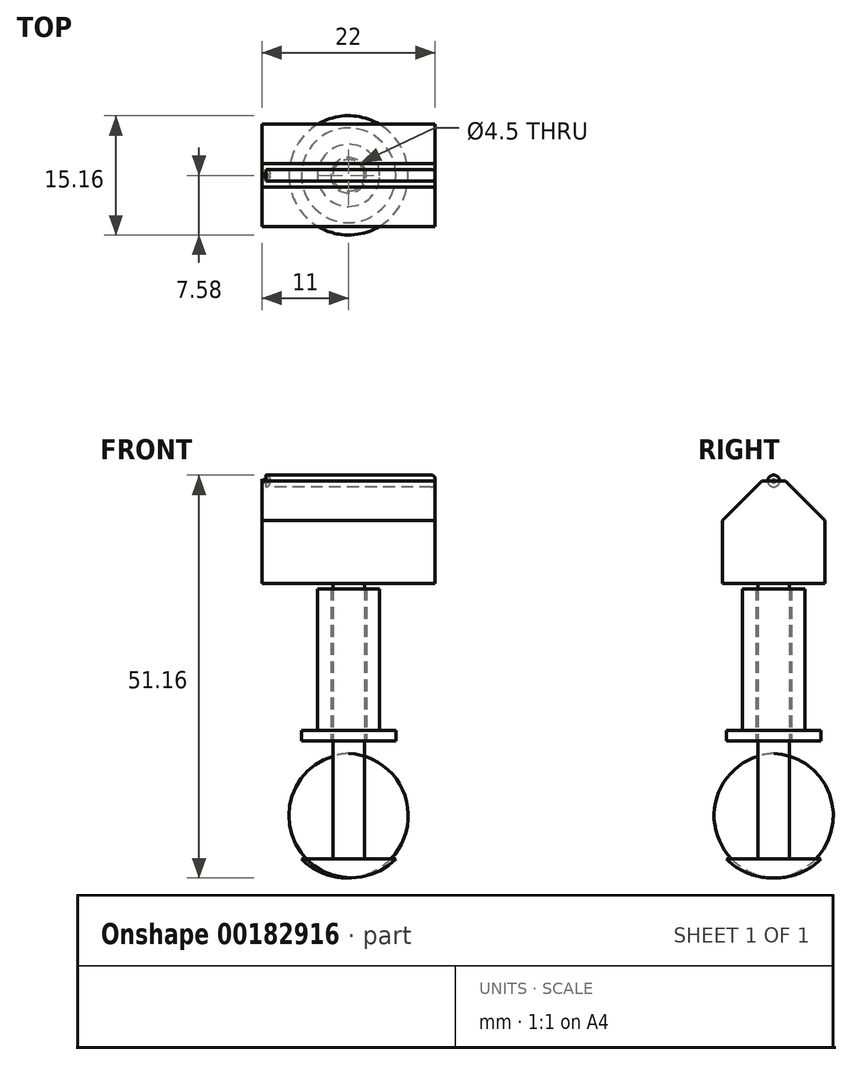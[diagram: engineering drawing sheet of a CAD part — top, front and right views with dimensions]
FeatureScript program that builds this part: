
annotation { "Feature Type Name" : "Feature", "Feature Type Description" : "" }
export const myFeature = defineFeature(function(context is Context, id is Id, definition is map)
    precondition{}
    {
        {
            var Q0;
            Q0=qCreatedBy(makeId("Top.planeOp"),FACE);
            var sketch = newSketch(context, id + "F0", { "sketchPlane" : qUnion([Q0])});
            skCircle(sketch, "E0", {"center": v(0, 0) * mm, "radius": 2 * mm});
            skSolve(sketch);
        }
        {
            var Q0;
            Q0 = qSketchRegion(id + "F0", true);
            extrude(context, id + "F1", {"entities" : qUnion([Q0]), "depth" : 40 * mm});
        }
        {
            var Q0;
            Q0=qCreatedBy(makeId("Right.planeOp"),FACE);
            var sketch = newSketch(context, id + "F2", { "sketchPlane" : qUnion([Q0])});
            skLineSegment(sketch, "E1", {"start": v(0, 0) * mm, "end": v(-6, 0) * mm});
            skLineSegment(sketch, "E2", {"start": v(0, 0) * mm, "end": v(0, -2.4) * mm});
            skArc(sketch, "E3", {"start": v(-6, 0) * mm, "mid": v(-3.26, -1.84) * mm, "end": v(0, -2.4) * mm});
            skSolve(sketch);
        }
        {
            var Q0;
            Q0=makeQuery(id+"F2.imprint","IMPRINT",FACE,{"disambiguationData":[TD([[makeQuery(id+"F2.imprint","IMPRINT",EDGE,{"derivedFrom":sQuery(id+"F2.wireOp",EDGE,"E1")}),1.0]])]});
            var Q1;
            Q1=sQuery(id+"F2.wireOp",EDGE,"E2");
            revolve(context, id + "F3", {"operationType" : NewBodyOperationType.ADD, "entities" : qUnion([Q0]), "axis" : qUnion([Q1]), "revolveType" : RevolveType.FULL});
        }
        {
            var Q0;
            Q0=makeQuery(id+"F1.opExtrude","CAP_FACE",FACE,{"disambiguationData":[OSD([sQuery(id+"F0.wireOp",EDGE,"E0")])],"isStart":false});
            var sketch = newSketch(context, id + "F4", { "sketchPlane" : qUnion([Q0])});
            skLineSegment(sketch, "E4.bottom", {"start": v(11, -6.5) * mm, "end": v(-11, -6.5) * mm});
            skLineSegment(sketch, "E4.top", {"start": v(11, 6.5) * mm, "end": v(-11, 6.5) * mm});
            skLineSegment(sketch, "E4.left", {"start": v(11, -6.5) * mm, "end": v(11, 6.5) * mm});
            skLineSegment(sketch, "E4.right", {"start": v(-11, -6.5) * mm, "end": v(-11, 6.5) * mm});
            skPoint(sketch, "E4.middle", {"position": v(0, 0) * mm});
            skSolve(sketch);
        }
        {
            var Q0;
            Q0=makeQuery(id+"F4.imprint","IMPRINT",FACE,{"disambiguationData":[TD([[makeQuery(id+"F4.imprint","IMPRINT",EDGE,{"derivedFrom":sQuery(id+"F4.wireOp",EDGE,"E4.bottom")}),-1.0]])]});
            extrude(context, id + "F5", {"entities" : qUnion([Q0]), "oppositeDirection" : true, "depth" : 5 * mm});
        }
        {
            var Q0;
            Q0=makeQuery(id+"F5.opExtrude","CAP_FACE",FACE,{"disambiguationData":[OSD([sQuery(id+"F0.wireOp",EDGE,"E0"),sQuery(id+"F4.wireOp",EDGE,"E4.bottom"),sQuery(id+"F4.wireOp",EDGE,"E4.top"),sQuery(id+"F4.wireOp",EDGE,"E4.left"),sQuery(id+"F4.wireOp",EDGE,"E4.right")])],"isStart":true});
            var Q1;
            Q1=makeQuery(id+"F1.opExtrude","CAP_FACE",FACE,{"disambiguationData":[OSD([sQuery(id+"F0.wireOp",EDGE,"E0")])],"isStart":false});
            extrude(context, id + "F6", {"entities" : qUnion([Q0, Q1]), "operationType" : NewBodyOperationType.ADD, "depth" : 8 * mm});
        }
        {
            var Q0;
            Q0=makeQuery(id+"F6.opExtrude","CAP_EDGE",EDGE,{"disambiguationData":[OSD([sQuery(id+"F4.wireOp",EDGE,"E4.bottom")])],"isStart":false});
            var Q1;
            Q1=makeQuery(id+"F6.opExtrude","CAP_EDGE",EDGE,{"disambiguationData":[OSD([sQuery(id+"F4.wireOp",EDGE,"E4.top")])],"isStart":false});
            chamfer(context, id + "F7", {"entities" : qUnion([Q0, Q1]), "width" : 5 * mm, "tangentPropagation" : true});
        }
        {
            var Q0;
            Q0=qCreatedBy(makeId("Right.planeOp"),FACE);
            var sketch = newSketch(context, id + "F8", { "sketchPlane" : qUnion([Q0])});
            skCircle(sketch, "E5", {"center": v(0, 48) * mm, "radius": 0.75 * mm});
            skSolve(sketch);
        }
        {
            var Q0;
            Q0=makeQuery(id+"F8.imprint","IMPRINT",FACE,{"disambiguationData":[TD([[makeQuery(id+"F8.imprint","IMPRINT",EDGE,{"derivedFrom":sQuery(id+"F8.wireOp",EDGE,"E5")}),1.0]])]});
            extrude(context, id + "F9", {"entities" : qUnion([Q0]), "depth" : 11 * mm, "hasSecondDirection" : true, "secondDirectionOppositeDirection" : true, "secondDirectionDepth" : 11 * mm});
        }
        {
            var Q0;
            Q0=makeQuery(id+"F9.opExtrude","CAP_EDGE",EDGE,{"disambiguationData":[OSD([sQuery(id+"F8.wireOp",EDGE,"E5")])],"isStart":false});
            var Q1;
            Q1=makeQuery(id+"F9.opExtrude","CAP_EDGE",EDGE,{"disambiguationData":[OSD([sQuery(id+"F8.wireOp",EDGE,"E5")])],"isStart":true});
            fillet(context, id + "F10", {"entities" : qUnion([Q0, Q1]), "radius" : 0.5 * mm, "tangentPropagation" : true, "allowEdgeOverflow" : false});
        }
        {
            var Q0;
            Q0=qCreatedBy(makeId("Top.planeOp"),FACE);
            cPlane(context, id + "F11", {"entities" : qUnion([Q0]), "cplaneType" : CPlaneType.OFFSET, "offset" : 15 * mm, "width" : 150 * mm, "height" : 150 * mm});
        }
        {
            var Q0;
            Q0=qCreatedBy(id+"F11.planeOp",FACE);
            var sketch = newSketch(context, id + "F12", { "sketchPlane" : qUnion([Q0])});
            skCircle(sketch, "E6", {"center": v(0, 0) * mm, "radius": 6 * mm});
            skCircle(sketch, "E7", {"center": v(0, 0) * mm, "radius": 2.25 * mm});
            skSolve(sketch);
        }
        {
            var Q0;
            Q0=makeQuery(id+"F12.imprint","IMPRINT",FACE,{"disambiguationData":[TD([[makeQuery(id+"F12.imprint","IMPRINT",EDGE,{"derivedFrom":sQuery(id+"F12.wireOp",EDGE,"E6")}),1.0]])]});
            extrude(context, id + "F13", {"entities" : qUnion([Q0]), "depth" : 1.3 * mm});
        }
        {
            var Q0;
            Q0=makeQuery(id+"F13.opExtrude","CAP_FACE",FACE,{"disambiguationData":[OSD([sQuery(id+"F12.wireOp",EDGE,"E6")])],"isStart":false});
            var sketch = newSketch(context, id + "F14", { "sketchPlane" : qUnion([Q0])});
            skCircle(sketch, "E8", {"center": v(0, 0) * mm, "radius": 2.25 * mm});
            skCircle(sketch, "E9", {"center": v(0, 0) * mm, "radius": 3.95 * mm});
            skSolve(sketch);
        }
        {
            var Q0;
            Q0=makeQuery(id+"F14.imprint","IMPRINT",FACE,{"disambiguationData":[TD([[makeQuery(id+"F14.imprint","IMPRINT",EDGE,{"derivedFrom":sQuery(id+"F14.wireOp",EDGE,"E8")}),-1.0]])]});
            extrude(context, id + "F15", {"entities" : qUnion([Q0]), "operationType" : NewBodyOperationType.ADD, "depth" : 18 * mm});
        }
    });
